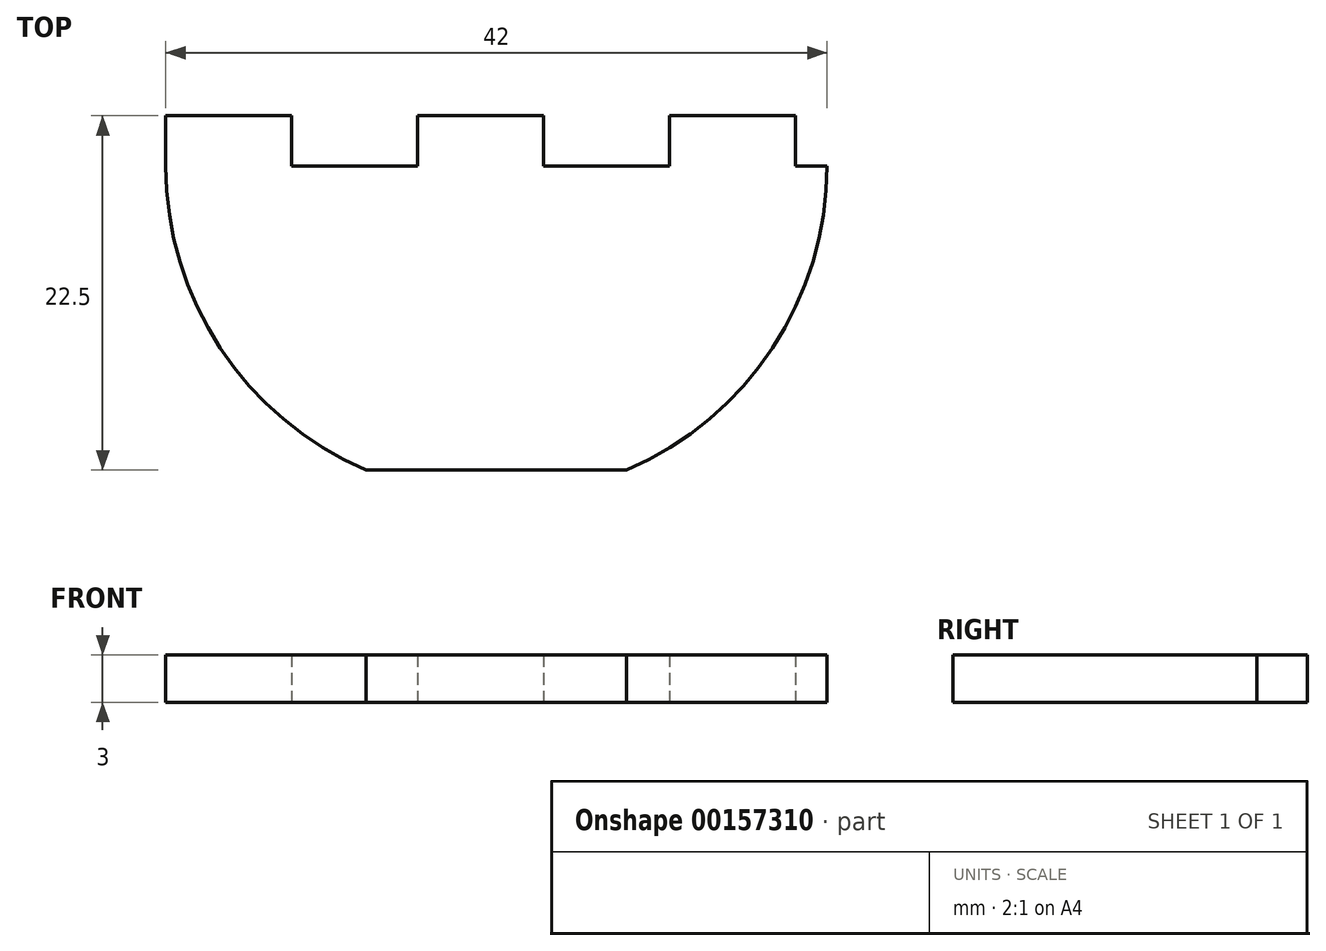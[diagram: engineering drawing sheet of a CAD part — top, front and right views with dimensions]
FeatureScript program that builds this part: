
annotation { "Feature Type Name" : "Feature", "Feature Type Description" : "" }
export const myFeature = defineFeature(function(context is Context, id is Id, definition is map)
    precondition{}
    {
        {
            var Q0;
            Q0=qCreatedBy(makeId("Top.planeOp"),FACE);
            var sketch = newSketch(context, id + "F0", { "sketchPlane" : qUnion([Q0])});
            skArc(sketch, "E0", {"start": v(-21, 0) * mm, "mid": v(-20.12, -6) * mm, "end": v(-17.57, -11.5) * mm});
            skLineSegment(sketch, "E1", {"start": v(-21, 0) * mm, "end": v(-21, 3.2) * mm});
            skLineSegment(sketch, "E2", {"start": v(-21, 3.2) * mm, "end": v(-13, 3.2) * mm});
            skLineSegment(sketch, "E3", {"start": v(-13, 3.2) * mm, "end": v(-13, 0) * mm});
            skLineSegment(sketch, "E4", {"start": v(-13, 0) * mm, "end": v(-5, 0) * mm});
            skLineSegment(sketch, "E5", {"start": v(-5, 0) * mm, "end": v(-5, 3.2) * mm});
            skLineSegment(sketch, "E6", {"start": v(-5, 3.2) * mm, "end": v(3, 3.2) * mm});
            skLineSegment(sketch, "E7", {"start": v(3, 3.2) * mm, "end": v(3, 0) * mm});
            skLineSegment(sketch, "E8", {"start": v(3, 0) * mm, "end": v(11, 0) * mm});
            skLineSegment(sketch, "E9", {"start": v(11, 0) * mm, "end": v(11, 3.2) * mm});
            skLineSegment(sketch, "E10", {"start": v(11, 3.2) * mm, "end": v(19, 3.2) * mm});
            skLineSegment(sketch, "E11", {"start": v(19, 3.2) * mm, "end": v(19, 0) * mm});
            skLineSegment(sketch, "E12", {"start": v(19, 0) * mm, "end": v(21, 0) * mm});
            skLineSegment(sketch, "E13", {"start": v(0, 0) * mm, "end": v(0, -21) * mm, "construction": true});
            skLineSegment(sketch, "E14", {"start": v(0, -21) * mm, "end": v(0, -11.5) * mm, "construction": true});
            skArc(sketch, "E15.trimOffspring", {"start": v(17.57, -11.5) * mm, "mid": v(20.12, -6) * mm, "end": v(21, 0) * mm});
            skLineSegment(sketch, "E16", {"start": v(0, 0) * mm, "end": v(0, -19.3) * mm, "construction": true});
            skArc(sketch, "E17", {"start": v(-21, 0) * mm, "mid": v(-17.53, -11.56) * mm, "end": v(-8.28, -19.3) * mm});
            skLineSegment(sketch, "E18", {"start": v(-8.28, -19.3) * mm, "end": v(8.28, -19.3) * mm});
            skArc(sketch, "E19.trimOffspring", {"start": v(8.28, -19.3) * mm, "mid": v(13.5, -16.09) * mm, "end": v(17.57, -11.5) * mm});
            skSolve(sketch);
        }
        {
            var Q0;
            Q0 = qSketchRegion(id + "F0", true);
            extrude(context, id + "F1", {"entities" : qUnion([Q0]), "depth" : 3 * mm});
        }
    });
